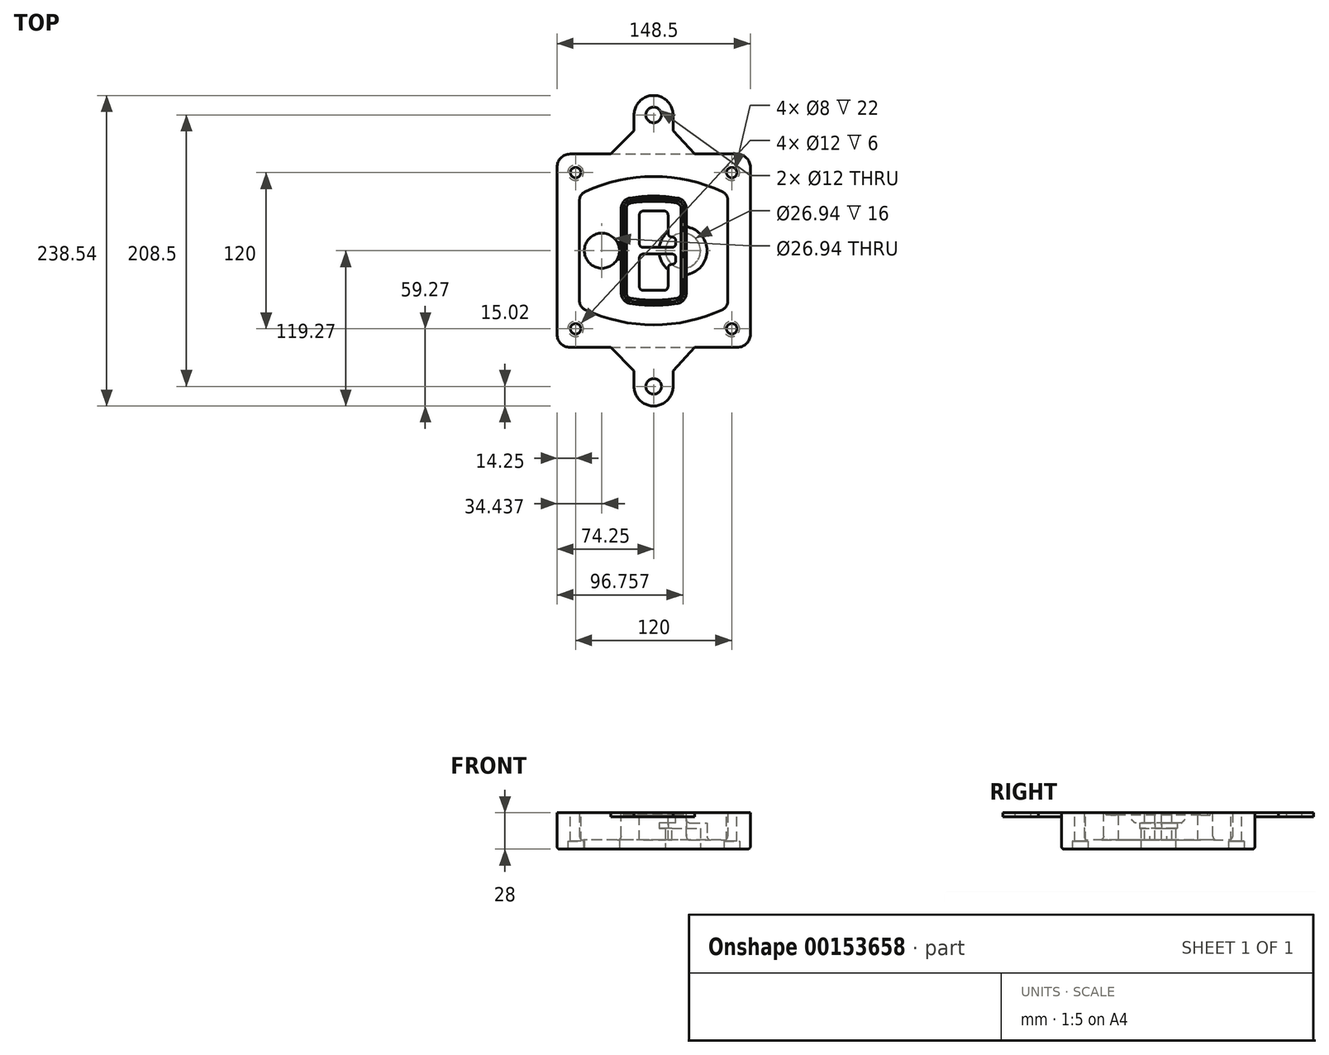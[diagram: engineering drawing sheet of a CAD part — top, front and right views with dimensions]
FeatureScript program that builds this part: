
annotation { "Feature Type Name" : "Feature", "Feature Type Description" : "" }
export const myFeature = defineFeature(function(context is Context, id is Id, definition is map)
    precondition{}
    {
        {
            var Q0;
            Q0=qCreatedBy(makeId("Top.planeOp"),FACE);
            var sketch = newSketch(context, id + "F0", { "sketchPlane" : qUnion([Q0])});
            skPoint(sketch, "E0.rect.middle", {"position": v(0, 0) * mm});
            skLineSegment(sketch, "E1.bottom", {"start": v(-64.25, -74.25) * mm, "end": v(64.25, -74.25) * mm});
            skLineSegment(sketch, "E1.top", {"start": v(-64.25, 74.25) * mm, "end": v(64.25, 74.25) * mm});
            skLineSegment(sketch, "E1.left", {"start": v(-74.25, -64.25) * mm, "end": v(-74.25, 64.25) * mm});
            skLineSegment(sketch, "E1.right", {"start": v(74.25, -64.25) * mm, "end": v(74.25, 64.25) * mm});
            skLineSegment(sketch, "E2", {"start": v(-74.25, 74.25) * mm, "end": v(74.25, -74.25) * mm, "construction": true});
            skLineSegment(sketch, "E3", {"start": v(74.25, 74.25) * mm, "end": v(-74.25, -74.25) * mm, "construction": true});
            skCircle(sketch, "E4", {"center": v(-60, 60) * mm, "radius": 4 * mm});
            skCircle(sketch, "E5", {"center": v(60, 60) * mm, "radius": 4 * mm});
            skCircle(sketch, "E6", {"center": v(60, -60) * mm, "radius": 4 * mm});
            skCircle(sketch, "E7", {"center": v(-60, -60) * mm, "radius": 4 * mm});
            skLineSegment(sketch, "E8", {"start": v(-60, 60) * mm, "end": v(60, 60) * mm, "construction": true});
            skLineSegment(sketch, "E9", {"start": v(60, 60) * mm, "end": v(60, -60) * mm, "construction": true});
            skLineSegment(sketch, "E10", {"start": v(60, -60) * mm, "end": v(-60, -60) * mm, "construction": true});
            skLineSegment(sketch, "E11", {"start": v(-60, -60) * mm, "end": v(-60, 60) * mm, "construction": true});
            skLineSegment(sketch, "E12", {"start": v(-60, 38.83) * mm, "end": v(-60, -38.83) * mm});
            skLineSegment(sketch, "E13", {"start": v(60, 38.83) * mm, "end": v(60, -38.83) * mm});
            skArc(sketch, "E14", {"start": v(54.26, 47.88) * mm, "mid": v(0, 60) * mm, "end": v(-54.26, 47.88) * mm});
            skArc(sketch, "E15", {"start": v(-54.26, -47.88) * mm, "mid": v(0, -60) * mm, "end": v(54.26, -47.88) * mm});
            skLineSegment(sketch, "E16", {"start": v(-60, 0) * mm, "end": v(60, 0) * mm, "construction": true});
            skPoint(sketch, "E17.visualSharp", {"position": v(-60, -45) * mm});
            skArc(sketch, "E17.filletArc", {"start": v(-60, -38.83) * mm, "mid": v(-58.44, -44.2) * mm, "end": v(-54.26, -47.88) * mm});
            skPoint(sketch, "E18.visualSharp", {"position": v(-60, 45) * mm});
            skArc(sketch, "E18.filletArc", {"start": v(-54.26, 47.88) * mm, "mid": v(-58.44, 44.2) * mm, "end": v(-60, 38.83) * mm});
            skPoint(sketch, "E19.visualSharp", {"position": v(60, 45) * mm});
            skArc(sketch, "E19.filletArc", {"start": v(60, 38.83) * mm, "mid": v(58.44, 44.2) * mm, "end": v(54.26, 47.88) * mm});
            skPoint(sketch, "E20.visualSharp", {"position": v(60, -45) * mm});
            skArc(sketch, "E20.filletArc", {"start": v(54.26, -47.88) * mm, "mid": v(58.44, -44.2) * mm, "end": v(60, -38.83) * mm});
            skPoint(sketch, "E21.visualSharp", {"position": v(-74.25, 74.25) * mm});
            skArc(sketch, "E21.filletArc", {"start": v(-64.25, 74.25) * mm, "mid": v(-71.32, 71.32) * mm, "end": v(-74.25, 64.25) * mm});
            skPoint(sketch, "E22.visualSharp", {"position": v(74.25, 74.25) * mm});
            skArc(sketch, "E22.filletArc", {"start": v(74.25, 64.25) * mm, "mid": v(71.32, 71.32) * mm, "end": v(64.25, 74.25) * mm});
            skPoint(sketch, "E23.visualSharp", {"position": v(74.25, -74.25) * mm});
            skArc(sketch, "E23.filletArc", {"start": v(64.25, -74.25) * mm, "mid": v(71.32, -71.32) * mm, "end": v(74.25, -64.25) * mm});
            skPoint(sketch, "E24.visualSharp", {"position": v(-74.25, -74.25) * mm});
            skArc(sketch, "E24.filletArc", {"start": v(-74.25, -64.25) * mm, "mid": v(-71.32, -71.32) * mm, "end": v(-64.25, -74.25) * mm});
            skArc(sketch, "E25.0", {"start": v(57, 38.83) * mm, "mid": v(55.9, 42.58) * mm, "end": v(52.98, 45.17) * mm});
            skLineSegment(sketch, "E25.1", {"start": v(57, 38.83) * mm, "end": v(57, -38.83) * mm});
            skArc(sketch, "E25.2", {"start": v(52.98, -45.17) * mm, "mid": v(55.9, -42.58) * mm, "end": v(57, -38.83) * mm});
            skArc(sketch, "E25.3", {"start": v(-52.98, -45.17) * mm, "mid": v(0, -57) * mm, "end": v(52.98, -45.17) * mm});
            skArc(sketch, "E25.4", {"start": v(-57, -38.83) * mm, "mid": v(-55.9, -42.58) * mm, "end": v(-52.98, -45.17) * mm});
            skArc(sketch, "E25.5", {"start": v(52.98, 45.17) * mm, "mid": v(0, 57) * mm, "end": v(-52.98, 45.17) * mm});
            skLineSegment(sketch, "E25.6", {"start": v(-57, 38.83) * mm, "end": v(-57, -38.83) * mm});
            skArc(sketch, "E25.7", {"start": v(-52.98, 45.17) * mm, "mid": v(-55.9, 42.58) * mm, "end": v(-57, 38.83) * mm});
            skArc(sketch, "E26.0", {"start": v(-55.96, 51.5) * mm, "mid": v(-61.82, 46.33) * mm, "end": v(-64, 38.83) * mm});
            skArc(sketch, "E26.1", {"start": v(55.96, 51.5) * mm, "mid": v(0, 64) * mm, "end": v(-55.96, 51.5) * mm});
            skArc(sketch, "E26.2", {"start": v(64, 38.83) * mm, "mid": v(61.82, 46.33) * mm, "end": v(55.96, 51.5) * mm});
            skLineSegment(sketch, "E26.3", {"start": v(64, 38.83) * mm, "end": v(64, -38.83) * mm});
            skArc(sketch, "E26.4", {"start": v(55.96, -51.5) * mm, "mid": v(61.82, -46.33) * mm, "end": v(64, -38.83) * mm});
            skLineSegment(sketch, "E26.5", {"start": v(-64, 38.83) * mm, "end": v(-64, -38.83) * mm});
            skArc(sketch, "E26.6", {"start": v(-55.96, -51.5) * mm, "mid": v(0, -64) * mm, "end": v(55.96, -51.5) * mm});
            skArc(sketch, "E26.7", {"start": v(-64, -38.83) * mm, "mid": v(-61.82, -46.33) * mm, "end": v(-55.96, -51.5) * mm});
            skSolve(sketch);
        }
        {
            var Q0;
            Q0=makeQuery(id+"F0.imprint","IMPRINT",FACE,{"disambiguationData":[TD([[makeQuery(id+"F0.imprint","IMPRINT",EDGE,{"derivedFrom":sQuery(id+"F0.wireOp",EDGE,"E1.bottom")}),1.0]])]});
            var Q1;
            Q1=makeQuery(id+"F0.imprint","IMPRINT",FACE,{"disambiguationData":[TD([[makeQuery(id+"F0.imprint","IMPRINT",EDGE,{"derivedFrom":sQuery(id+"F0.wireOp",EDGE,"E12")}),1.0]])]});
            var Q2;
            Q2=makeQuery(id+"F0.imprint","IMPRINT",FACE,{"disambiguationData":[TD([[makeQuery(id+"F0.imprint","IMPRINT",EDGE,{"derivedFrom":sQuery(id+"F0.wireOp",EDGE,"E25.0")}),1.0]])]});
            var Q3;
            Q3=makeQuery(id+"F0.imprint","IMPRINT",FACE,{"disambiguationData":[TD([[makeQuery(id+"F0.imprint","IMPRINT",EDGE,{"derivedFrom":sQuery(id+"F0.wireOp",EDGE,"E12")}),-1.0]])]});
            extrude(context, id + "F1", {"entities" : qUnion([Q0, Q1, Q2, Q3]), "oppositeDirection" : true, "depth" : 25 * mm});
        }
        {
            var Q0;
            Q0=makeQuery(id+"F0.imprint","IMPRINT",FACE,{"disambiguationData":[TD([[makeQuery(id+"F0.imprint","IMPRINT",EDGE,{"derivedFrom":sQuery(id+"F0.wireOp",EDGE,"E12")}),1.0]])]});
            extrude(context, id + "F2", {"entities" : qUnion([Q0]), "operationType" : NewBodyOperationType.ADD, "depth" : 3 * mm});
        }
        {
            var Q0;
            Q0=makeQuery(id+"F0.imprint","IMPRINT",FACE,{"disambiguationData":[TD([[makeQuery(id+"F0.imprint","IMPRINT",EDGE,{"derivedFrom":sQuery(id+"F0.wireOp",EDGE,"E25.0")}),1.0]])]});
            extrude(context, id + "F3", {"entities" : qUnion([Q0]), "operationType" : NewBodyOperationType.REMOVE, "oppositeDirection" : true, "depth" : 18 * mm});
        }
        {
            var Q0;
            Q0=makeQuery(id+"F2.opExtrude","CAP_FACE",FACE,{"disambiguationData":[OSD([sQuery(id+"F0.wireOp",EDGE,"E12"),sQuery(id+"F0.wireOp",EDGE,"E13"),sQuery(id+"F0.wireOp",EDGE,"E14"),sQuery(id+"F0.wireOp",EDGE,"E15"),sQuery(id+"F0.wireOp",EDGE,"E17.filletArc"),sQuery(id+"F0.wireOp",EDGE,"E18.filletArc"),sQuery(id+"F0.wireOp",EDGE,"E19.filletArc"),sQuery(id+"F0.wireOp",EDGE,"E20.filletArc"),sQuery(id+"F0.wireOp",EDGE,"E25.0"),sQuery(id+"F0.wireOp",EDGE,"E25.1"),sQuery(id+"F0.wireOp",EDGE,"E25.2"),sQuery(id+"F0.wireOp",EDGE,"E25.3"),sQuery(id+"F0.wireOp",EDGE,"E25.4"),sQuery(id+"F0.wireOp",EDGE,"E25.5"),sQuery(id+"F0.wireOp",EDGE,"E25.6"),sQuery(id+"F0.wireOp",EDGE,"E25.7")])],"isStart":false});
            var sketch = newSketch(context, id + "F4", { "sketchPlane" : qUnion([Q0])});
            skArc(sketch, "E27.0", {"start": v(-18.34, -40.45) * mm, "mid": v(0, -42) * mm, "end": v(18.34, -40.45) * mm});
            skArc(sketch, "E28.0", {"start": v(18.34, 40.45) * mm, "mid": v(0, 42) * mm, "end": v(-18.34, 40.45) * mm});
            skLineSegment(sketch, "E29", {"start": v(-25, 32.57) * mm, "end": v(-25, -32.57) * mm});
            skLineSegment(sketch, "E30", {"start": v(25, 32.57) * mm, "end": v(25, -32.57) * mm});
            skLineSegment(sketch, "E31", {"start": v(-25, 39.1) * mm, "end": v(25, 39.1) * mm, "construction": true});
            skLineSegment(sketch, "E32", {"start": v(-25, -39.1) * mm, "end": v(25, -39.1) * mm, "construction": true});
            skPoint(sketch, "E33.visualSharp", {"position": v(-25, 39.1) * mm});
            skArc(sketch, "E33.filletArc", {"start": v(-18.34, 40.45) * mm, "mid": v(-23.11, 37.73) * mm, "end": v(-25, 32.57) * mm});
            skPoint(sketch, "E34.visualSharp", {"position": v(25, 39.1) * mm});
            skArc(sketch, "E34.filletArc", {"start": v(25, 32.57) * mm, "mid": v(23.11, 37.73) * mm, "end": v(18.34, 40.45) * mm});
            skPoint(sketch, "E35.visualSharp", {"position": v(25, -39.1) * mm});
            skArc(sketch, "E35.filletArc", {"start": v(18.34, -40.45) * mm, "mid": v(23.11, -37.73) * mm, "end": v(25, -32.57) * mm});
            skPoint(sketch, "E36.visualSharp", {"position": v(-25, -39.1) * mm});
            skArc(sketch, "E36.filletArc", {"start": v(-25, -32.57) * mm, "mid": v(-23.11, -37.73) * mm, "end": v(-18.34, -40.45) * mm});
            skArc(sketch, "E37.0", {"start": v(52.98, 45.17) * mm, "mid": v(0, 57) * mm, "end": v(-52.98, 45.17) * mm});
            skArc(sketch, "E37.1", {"start": v(-52.98, 45.17) * mm, "mid": v(-55.9, 42.58) * mm, "end": v(-57, 38.83) * mm});
            skLineSegment(sketch, "E37.2", {"start": v(-57, 38.83) * mm, "end": v(-57, -38.83) * mm});
            skArc(sketch, "E37.3", {"start": v(-57, -38.83) * mm, "mid": v(-55.9, -42.58) * mm, "end": v(-52.98, -45.17) * mm});
            skArc(sketch, "E37.4", {"start": v(-52.98, -45.17) * mm, "mid": v(0, -57) * mm, "end": v(52.98, -45.17) * mm});
            skArc(sketch, "E37.5", {"start": v(52.98, -45.17) * mm, "mid": v(55.9, -42.58) * mm, "end": v(57, -38.83) * mm});
            skLineSegment(sketch, "E37.6", {"start": v(57, 38.83) * mm, "end": v(57, -38.83) * mm});
            skArc(sketch, "E37.7", {"start": v(57, 38.83) * mm, "mid": v(55.9, 42.58) * mm, "end": v(52.98, 45.17) * mm});
            skLineSegment(sketch, "E38.0", {"start": v(23, 32.57) * mm, "end": v(23, -32.57) * mm});
            skArc(sketch, "E38.1", {"start": v(18, -38.48) * mm, "mid": v(21.58, -36.44) * mm, "end": v(23, -32.57) * mm});
            skArc(sketch, "E38.2", {"start": v(-18, -38.48) * mm, "mid": v(0, -40) * mm, "end": v(18, -38.48) * mm});
            skArc(sketch, "E38.3", {"start": v(-23, -32.57) * mm, "mid": v(-21.58, -36.44) * mm, "end": v(-18, -38.48) * mm});
            skLineSegment(sketch, "E38.4", {"start": v(-23, 32.57) * mm, "end": v(-23, -32.57) * mm});
            skArc(sketch, "E38.5", {"start": v(23, 32.57) * mm, "mid": v(21.58, 36.44) * mm, "end": v(18, 38.48) * mm});
            skArc(sketch, "E38.6", {"start": v(-18, 38.48) * mm, "mid": v(-21.58, 36.44) * mm, "end": v(-23, 32.57) * mm});
            skArc(sketch, "E38.7", {"start": v(18, 38.48) * mm, "mid": v(0, 40) * mm, "end": v(-18, 38.48) * mm});
            skArc(sketch, "E39.0", {"start": v(21, 32.57) * mm, "mid": v(20.06, 35.15) * mm, "end": v(17.67, 36.5) * mm});
            skLineSegment(sketch, "E39.1", {"start": v(21, 32.57) * mm, "end": v(21, -32.57) * mm});
            skArc(sketch, "E39.2", {"start": v(17.67, -36.5) * mm, "mid": v(20.06, -35.15) * mm, "end": v(21, -32.57) * mm});
            skArc(sketch, "E39.3", {"start": v(-17.67, -36.5) * mm, "mid": v(0, -38) * mm, "end": v(17.67, -36.5) * mm});
            skArc(sketch, "E39.4", {"start": v(-21, -32.57) * mm, "mid": v(-20.06, -35.15) * mm, "end": v(-17.67, -36.5) * mm});
            skArc(sketch, "E39.5", {"start": v(17.67, 36.5) * mm, "mid": v(0, 38) * mm, "end": v(-17.67, 36.5) * mm});
            skLineSegment(sketch, "E39.6", {"start": v(-21, 32.57) * mm, "end": v(-21, -32.57) * mm});
            skArc(sketch, "E39.7", {"start": v(-17.67, 36.5) * mm, "mid": v(-20.06, 35.15) * mm, "end": v(-21, 32.57) * mm});
            skLineSegment(sketch, "E40", {"start": v(-25, 0) * mm, "end": v(25, 0) * mm, "construction": true});
            skLineSegment(sketch, "E41", {"start": v(-11, 5.5) * mm, "end": v(-11, 27.5) * mm});
            skLineSegment(sketch, "E42", {"start": v(-8, 30.5) * mm, "end": v(8, 30.5) * mm});
            skLineSegment(sketch, "E43", {"start": v(11, 27.5) * mm, "end": v(11, 13.5) * mm});
            skLineSegment(sketch, "E44", {"start": v(14, 10.5) * mm, "end": v(14, 10.5) * mm});
            skLineSegment(sketch, "E45", {"start": v(17, 7.5) * mm, "end": v(17, 5.5) * mm});
            skLineSegment(sketch, "E46", {"start": v(14, 2.5) * mm, "end": v(-8, 2.5) * mm});
            skPoint(sketch, "E47.visualSharp", {"position": v(-11, 30.5) * mm});
            skArc(sketch, "E47.filletArc", {"start": v(-8, 30.5) * mm, "mid": v(-10.12, 29.62) * mm, "end": v(-11, 27.5) * mm});
            skPoint(sketch, "E48.visualSharp", {"position": v(11, 30.5) * mm});
            skArc(sketch, "E48.filletArc", {"start": v(11, 27.5) * mm, "mid": v(10.12, 29.62) * mm, "end": v(8, 30.5) * mm});
            skPoint(sketch, "E49.visualSharp", {"position": v(11, 10.5) * mm});
            skArc(sketch, "E49.filletArc", {"start": v(11, 13.5) * mm, "mid": v(11.88, 11.38) * mm, "end": v(14, 10.5) * mm});
            skPoint(sketch, "E50.visualSharp", {"position": v(17, 10.5) * mm});
            skArc(sketch, "E50.filletArc", {"start": v(17, 7.5) * mm, "mid": v(16.12, 9.62) * mm, "end": v(14, 10.5) * mm});
            skPoint(sketch, "E51.visualSharp", {"position": v(17, 2.5) * mm});
            skArc(sketch, "E51.filletArc", {"start": v(14, 2.5) * mm, "mid": v(16.12, 3.38) * mm, "end": v(17, 5.5) * mm});
            skPoint(sketch, "E52.visualSharp", {"position": v(-11, 2.5) * mm});
            skArc(sketch, "E52.filletArc", {"start": v(-11, 5.5) * mm, "mid": v(-10.12, 3.38) * mm, "end": v(-8, 2.5) * mm});
            skLineSegment(sketch, "E53.0.MirrorCS", {"start": v(14, -2.5) * mm, "end": v(-8, -2.5) * mm});
            skArc(sketch, "E54.0.MirrorCS", {"start": v(-11, -5.5) * mm, "mid": v(-10.12, -3.38) * mm, "end": v(-8, -2.5) * mm});
            skLineSegment(sketch, "E55.0.MirrorCS", {"start": v(-11, -5.5) * mm, "end": v(-11, -27.5) * mm});
            skArc(sketch, "E56.0.MirrorCS", {"start": v(-8, -30.5) * mm, "mid": v(-10.12, -29.62) * mm, "end": v(-11, -27.5) * mm});
            skLineSegment(sketch, "E57.0.MirrorCS", {"start": v(-8, -30.5) * mm, "end": v(8, -30.5) * mm});
            skArc(sketch, "E58.0.MirrorCS", {"start": v(11, -27.5) * mm, "mid": v(10.12, -29.62) * mm, "end": v(8, -30.5) * mm});
            skLineSegment(sketch, "E59.0.MirrorCS", {"start": v(11, -27.5) * mm, "end": v(11, -13.5) * mm});
            skArc(sketch, "E60.0.MirrorCS", {"start": v(11, -13.5) * mm, "mid": v(11.88, -11.38) * mm, "end": v(14, -10.5) * mm});
            skArc(sketch, "E61.0.MirrorCS", {"start": v(17, -7.5) * mm, "mid": v(16.12, -9.62) * mm, "end": v(14, -10.5) * mm});
            skLineSegment(sketch, "E62.0.MirrorCS", {"start": v(17, -7.5) * mm, "end": v(17, -5.5) * mm});
            skArc(sketch, "E63.0.MirrorCS", {"start": v(14, -2.5) * mm, "mid": v(16.12, -3.38) * mm, "end": v(17, -5.5) * mm});
            skSolve(sketch);
        }
        {
            var Q0;
            Q0=makeQuery(id+"F4.imprint","IMPRINT",FACE,{"disambiguationData":[TD([[makeQuery(id+"F4.imprint","IMPRINT",EDGE,{"derivedFrom":sQuery(id+"F4.wireOp",EDGE,"E27.0")}),1.0]])]});
            var Q1;
            Q1=makeQuery(id+"F4.imprint","IMPRINT",FACE,{"disambiguationData":[TD([[makeQuery(id+"F4.imprint","IMPRINT",EDGE,{"derivedFrom":sQuery(id+"F4.wireOp",EDGE,"E38.0")}),-1.0]])]});
            var Q2;
            Q2=makeQuery(id+"F4.imprint","IMPRINT",FACE,{"disambiguationData":[TD([[makeQuery(id+"F4.imprint","IMPRINT",EDGE,{"derivedFrom":sQuery(id+"F4.wireOp",EDGE,"E39.0")}),1.0]])]});
            extrude(context, id + "F5", {"entities" : qUnion([Q0, Q1, Q2]), "operationType" : NewBodyOperationType.ADD, "endBound" : BoundingType.UP_TO_NEXT, "oppositeDirection" : true, "depth" : 25 * mm});
        }
        {
            var Q0;
            Q0=makeQuery(id+"F4.imprint","IMPRINT",FACE,{"disambiguationData":[TD([[makeQuery(id+"F4.imprint","IMPRINT",EDGE,{"derivedFrom":sQuery(id+"F4.wireOp",EDGE,"E38.0")}),-1.0]])]});
            extrude(context, id + "F6", {"entities" : qUnion([Q0]), "operationType" : NewBodyOperationType.REMOVE, "oppositeDirection" : true, "depth" : 2 * mm});
        }
        {
            var Q0;
            Q0=makeQuery(id+"F1.opExtrude","CAP_FACE",FACE,{"disambiguationData":[OSD([sQuery(id+"F0.wireOp",EDGE,"E1.bottom"),sQuery(id+"F0.wireOp",EDGE,"E1.top"),sQuery(id+"F0.wireOp",EDGE,"E1.left"),sQuery(id+"F0.wireOp",EDGE,"E1.right"),sQuery(id+"F0.wireOp",EDGE,"E4"),sQuery(id+"F0.wireOp",EDGE,"E5"),sQuery(id+"F0.wireOp",EDGE,"E6"),sQuery(id+"F0.wireOp",EDGE,"E7"),sQuery(id+"F0.wireOp",EDGE,"E21.filletArc"),sQuery(id+"F0.wireOp",EDGE,"E22.filletArc"),sQuery(id+"F0.wireOp",EDGE,"E23.filletArc"),sQuery(id+"F0.wireOp",EDGE,"E24.filletArc")])],"isStart":false});
            var sketch = newSketch(context, id + "F7", { "sketchPlane" : qUnion([Q0])});
            skCircle(sketch, "E64", {"center": v(22.5, 0) * mm, "radius": 13.47 * mm});
            skCircle(sketch, "E65", {"center": v(-39.81, 0) * mm, "radius": 13.47 * mm});
            skLineSegment(sketch, "E66", {"start": v(74.25, 0) * mm, "end": v(-74.25, 0) * mm});
            skCircle(sketch, "E67", {"center": v(22.5, 0) * mm, "radius": 18.47 * mm});
            skCircle(sketch, "E68", {"center": v(60, -60) * mm, "radius": 6 * mm});
            skCircle(sketch, "E69", {"center": v(-60, -60) * mm, "radius": 6 * mm});
            skCircle(sketch, "E70", {"center": v(-60, 60) * mm, "radius": 6 * mm});
            skCircle(sketch, "E71", {"center": v(60, 60) * mm, "radius": 6 * mm});
            skSolve(sketch);
        }
        {
            var Q0;
            {var subQ1=sQuery(id+"F7.wireOp",EDGE,"E66");var subQ4=sQuery(id+"F7.wireOp",EDGE,"E64");var subQ6=makeQuery(id+"F7.imprint","INTERSECT",VERTEX,{"disambiguationData":[OD(0.0)],"derivedFrom":[subQ4,subQ1]});Q0=makeQuery(id+"F7.imprint","IMPRINT",FACE,{"disambiguationData":[TD([[makeQuery(id+"F7.imprint","IMPRINT",EDGE,{"disambiguationData":[TD([[subQ6,-1.0]])],"derivedFrom":subQ4}),-1.0]])]});}
            var Q1;
            {var subQ0=sQuery(id+"F7.wireOp",EDGE,"E66");var subQ1=sQuery(id+"F7.wireOp",EDGE,"E64");var subQ3=makeQuery(id+"F7.imprint","INTERSECT",VERTEX,{"disambiguationData":[OD(0.0)],"derivedFrom":[subQ1,subQ0]});Q1=makeQuery(id+"F7.imprint","IMPRINT",FACE,{"disambiguationData":[TD([[makeQuery(id+"F7.imprint","IMPRINT",EDGE,{"disambiguationData":[TD([[subQ3,-1.0]])],"derivedFrom":subQ1}),1.0]])]});}
            var Q2;
            {var subQ0=sQuery(id+"F7.wireOp",EDGE,"E66");var subQ1=sQuery(id+"F7.wireOp",EDGE,"E64");var subQ3=makeQuery(id+"F7.imprint","INTERSECT",VERTEX,{"disambiguationData":[OD(0.0)],"derivedFrom":[subQ1,subQ0]});Q2=makeQuery(id+"F7.imprint","IMPRINT",FACE,{"disambiguationData":[TD([[makeQuery(id+"F7.imprint","IMPRINT",EDGE,{"disambiguationData":[TD([[subQ3,1.0]])],"derivedFrom":subQ1}),1.0]])]});}
            var Q3;
            {var subQ1=sQuery(id+"F7.wireOp",EDGE,"E66");var subQ4=sQuery(id+"F7.wireOp",EDGE,"E64");var subQ6=makeQuery(id+"F7.imprint","INTERSECT",VERTEX,{"disambiguationData":[OD(0.0)],"derivedFrom":[subQ4,subQ1]});Q3=makeQuery(id+"F7.imprint","IMPRINT",FACE,{"disambiguationData":[TD([[makeQuery(id+"F7.imprint","IMPRINT",EDGE,{"disambiguationData":[TD([[subQ6,1.0]])],"derivedFrom":subQ4}),-1.0]])]});}
            extrude(context, id + "F8", {"entities" : qUnion([Q0, Q1, Q2, Q3]), "operationType" : NewBodyOperationType.ADD, "oppositeDirection" : true, "depth" : 20 * mm});
        }
        {
            var Q0;
            {var subQ0=sQuery(id+"F7.wireOp",EDGE,"E66");var subQ1=sQuery(id+"F7.wireOp",EDGE,"E64");var subQ3=makeQuery(id+"F7.imprint","INTERSECT",VERTEX,{"disambiguationData":[OD(0.0)],"derivedFrom":[subQ1,subQ0]});Q0=makeQuery(id+"F7.imprint","IMPRINT",FACE,{"disambiguationData":[TD([[makeQuery(id+"F7.imprint","IMPRINT",EDGE,{"disambiguationData":[TD([[subQ3,-1.0]])],"derivedFrom":subQ1}),1.0]])]});}
            var Q1;
            {var subQ0=sQuery(id+"F7.wireOp",EDGE,"E66");var subQ1=sQuery(id+"F7.wireOp",EDGE,"E64");var subQ3=makeQuery(id+"F7.imprint","INTERSECT",VERTEX,{"disambiguationData":[OD(0.0)],"derivedFrom":[subQ1,subQ0]});Q1=makeQuery(id+"F7.imprint","IMPRINT",FACE,{"disambiguationData":[TD([[makeQuery(id+"F7.imprint","IMPRINT",EDGE,{"disambiguationData":[TD([[subQ3,1.0]])],"derivedFrom":subQ1}),1.0]])]});}
            extrude(context, id + "F9", {"entities" : qUnion([Q0, Q1]), "operationType" : NewBodyOperationType.REMOVE, "oppositeDirection" : true, "depth" : 16 * mm});
        }
        {
            var Q0;
            {var subQ0=sQuery(id+"F7.wireOp",EDGE,"E66");var subQ1=sQuery(id+"F7.wireOp",EDGE,"E65");var subQ3=makeQuery(id+"F7.imprint","INTERSECT",VERTEX,{"disambiguationData":[OD(0.0)],"derivedFrom":[subQ1,subQ0]});Q0=makeQuery(id+"F7.imprint","IMPRINT",FACE,{"disambiguationData":[TD([[makeQuery(id+"F7.imprint","IMPRINT",EDGE,{"disambiguationData":[TD([[subQ3,-1.0]])],"derivedFrom":subQ1}),1.0]])]});}
            var Q1;
            {var subQ0=sQuery(id+"F7.wireOp",EDGE,"E66");var subQ1=sQuery(id+"F7.wireOp",EDGE,"E65");var subQ3=makeQuery(id+"F7.imprint","INTERSECT",VERTEX,{"disambiguationData":[OD(0.0)],"derivedFrom":[subQ1,subQ0]});Q1=makeQuery(id+"F7.imprint","IMPRINT",FACE,{"disambiguationData":[TD([[makeQuery(id+"F7.imprint","IMPRINT",EDGE,{"disambiguationData":[TD([[subQ3,1.0]])],"derivedFrom":subQ1}),1.0]])]});}
            extrude(context, id + "F10", {"entities" : qUnion([Q0, Q1]), "operationType" : NewBodyOperationType.REMOVE, "oppositeDirection" : true, "depth" : 25 * mm});
        }
        {
            var Q0;
            Q0=makeQuery(id+"F7.imprint","IMPRINT",FACE,{"disambiguationData":[TD([[makeQuery(id+"F7.imprint","IMPRINT",EDGE,{"derivedFrom":sQuery(id+"F7.wireOp",EDGE,"E68")}),1.0]])]});
            var Q1;
            Q1=makeQuery(id+"F7.imprint","IMPRINT",FACE,{"disambiguationData":[TD([[makeQuery(id+"F7.imprint","IMPRINT",EDGE,{"derivedFrom":makeQuery(id+"F1.opExtrude","CAP_EDGE",EDGE,{"disambiguationData":[OSD([sQuery(id+"F0.wireOp",EDGE,"E5")])],"isStart":false})}),-1.0]])]});
            var Q2;
            Q2=makeQuery(id+"F7.imprint","IMPRINT",FACE,{"disambiguationData":[TD([[makeQuery(id+"F7.imprint","IMPRINT",EDGE,{"derivedFrom":sQuery(id+"F7.wireOp",EDGE,"E69")}),1.0]])]});
            var Q3;
            Q3=makeQuery(id+"F7.imprint","IMPRINT",FACE,{"disambiguationData":[TD([[makeQuery(id+"F7.imprint","IMPRINT",EDGE,{"derivedFrom":makeQuery(id+"F1.opExtrude","CAP_EDGE",EDGE,{"disambiguationData":[OSD([sQuery(id+"F0.wireOp",EDGE,"E4")])],"isStart":false})}),-1.0]])]});
            var Q4;
            Q4=makeQuery(id+"F7.imprint","IMPRINT",FACE,{"disambiguationData":[TD([[makeQuery(id+"F7.imprint","IMPRINT",EDGE,{"derivedFrom":sQuery(id+"F7.wireOp",EDGE,"E70")}),1.0]])]});
            var Q5;
            Q5=makeQuery(id+"F7.imprint","IMPRINT",FACE,{"disambiguationData":[TD([[makeQuery(id+"F7.imprint","IMPRINT",EDGE,{"derivedFrom":makeQuery(id+"F1.opExtrude","CAP_EDGE",EDGE,{"disambiguationData":[OSD([sQuery(id+"F0.wireOp",EDGE,"E7")])],"isStart":false})}),-1.0]])]});
            var Q6;
            Q6=makeQuery(id+"F7.imprint","IMPRINT",FACE,{"disambiguationData":[TD([[makeQuery(id+"F7.imprint","IMPRINT",EDGE,{"derivedFrom":sQuery(id+"F7.wireOp",EDGE,"E71")}),1.0]])]});
            var Q7;
            Q7=makeQuery(id+"F7.imprint","IMPRINT",FACE,{"disambiguationData":[TD([[makeQuery(id+"F7.imprint","IMPRINT",EDGE,{"derivedFrom":makeQuery(id+"F1.opExtrude","CAP_EDGE",EDGE,{"disambiguationData":[OSD([sQuery(id+"F0.wireOp",EDGE,"E6")])],"isStart":false})}),-1.0]])]});
            extrude(context, id + "F11", {"entities" : qUnion([Q0, Q1, Q2, Q3, Q4, Q5, Q6, Q7]), "operationType" : NewBodyOperationType.REMOVE, "oppositeDirection" : true, "depth" : 6 * mm});
        }
        {
            var Q0;
            Q0=makeQuery(id+"F9.boolean.opBoolean","COPY",FACE,{"derivedFrom":makeQuery(id+"F9.opExtrude","CAP_FACE",FACE,{"disambiguationData":[OSD([sQuery(id+"F7.wireOp",EDGE,"E64")])],"isStart":false})});
            var sketch = newSketch(context, id + "F12", { "sketchPlane" : qUnion([Q0])});
            skArc(sketch, "E72.0", {"start": v(11, 14.45) * mm, "mid": v(6.45, 9.13) * mm, "end": v(4.2, 2.5) * mm});
            skArc(sketch, "E72.1", {"start": v(4.2, -2.5) * mm, "mid": v(6.45, -9.13) * mm, "end": v(11, -14.45) * mm});
            skLineSegment(sketch, "E73", {"start": v(4.2, -2.5) * mm, "end": v(14, -2.5) * mm});
            skLineSegment(sketch, "E74.0", {"start": v(14, 2.5) * mm, "end": v(4.2, 2.5) * mm});
            skArc(sketch, "E74.1", {"start": v(14, 2.5) * mm, "mid": v(16.12, 3.38) * mm, "end": v(17, 5.5) * mm});
            skLineSegment(sketch, "E74.2", {"start": v(17, 7.5) * mm, "end": v(17, 5.5) * mm});
            skArc(sketch, "E74.3", {"start": v(17, 7.5) * mm, "mid": v(16.12, 9.62) * mm, "end": v(14, 10.5) * mm});
            skArc(sketch, "E74.4", {"start": v(11, 13.5) * mm, "mid": v(11.88, 11.38) * mm, "end": v(14, 10.5) * mm});
            skLineSegment(sketch, "E74.5", {"start": v(11, 14.45) * mm, "end": v(11, 13.5) * mm});
            skLineSegment(sketch, "E74.7", {"start": v(14, -2.5) * mm, "end": v(4.2, -2.5) * mm});
            skArc(sketch, "E74.8", {"start": v(14, -2.5) * mm, "mid": v(16.12, -3.38) * mm, "end": v(17, -5.5) * mm});
            skLineSegment(sketch, "E74.9", {"start": v(17, -7.5) * mm, "end": v(17, -5.5) * mm});
            skArc(sketch, "E74.10", {"start": v(17, -7.5) * mm, "mid": v(16.12, -9.62) * mm, "end": v(14, -10.5) * mm});
            skArc(sketch, "E74.11", {"start": v(11, -13.5) * mm, "mid": v(11.88, -11.38) * mm, "end": v(14, -10.5) * mm});
            skLineSegment(sketch, "E74.12", {"start": v(11, -14.45) * mm, "end": v(11, -13.5) * mm});
            skPoint(sketch, "E75.orphan", {"position": v(11, -27.5) * mm});
            skPoint(sketch, "E76.orphan", {"position": v(-8, -2.5) * mm});
            skPoint(sketch, "E77.orphan", {"position": v(-8, 2.5) * mm});
            skPoint(sketch, "E78.orphan", {"position": v(11, 27.5) * mm});
            skSolve(sketch);
        }
        {
            var Q0;
            {var subQ7=sQuery(id+"F12.wireOp",EDGE,"E72.0");var subQ14=sQuery(id+"F12.wireOp",EDGE,"E72.1");var subQ16=sQuery(id+"F12.wireOp",EDGE,"E74.1");var subQ18=sQuery(id+"F12.wireOp",EDGE,"E74.8");Q0=qUnion([makeQuery(id+"F12.imprint","IMPRINT",FACE,{"disambiguationData":[TD([[makeQuery(id+"F12.imprint","IMPRINT",EDGE,{"derivedFrom":subQ7}),1.0]])]}),makeQuery(id+"F12.imprint","IMPRINT",FACE,{"disambiguationData":[TD([[makeQuery(id+"F12.imprint","IMPRINT",EDGE,{"derivedFrom":subQ14}),1.0]])]}),makeQuery(id+"F12.imprint","IMPRINT",FACE,{"disambiguationData":[TD([[makeQuery(id+"F12.imprint","IMPRINT",EDGE,{"derivedFrom":subQ16}),1.0]])]}),makeQuery(id+"F12.imprint","IMPRINT",FACE,{"disambiguationData":[TD([[makeQuery(id+"F12.imprint","IMPRINT",EDGE,{"derivedFrom":subQ18}),-1.0]])]})]);}
            var Q1;
            Q1=makeQuery(id+"F5.boolean.opBoolean","SPLIT",FACE,{"disambiguationData":[TD([makeQuery(id+"F5.opExtrude","SWEPT_FACE",FACE,{"disambiguationData":[OSD([sQuery(id+"F4.wireOp",EDGE,"E41")])]})])],"derivedFrom":makeQuery(id+"F3.boolean.opBoolean","COPY",FACE,{"derivedFrom":makeQuery(id+"F3.opExtrude","CAP_FACE",FACE,{"disambiguationData":[OSD([sQuery(id+"F0.wireOp",EDGE,"E25.0"),sQuery(id+"F0.wireOp",EDGE,"E25.1"),sQuery(id+"F0.wireOp",EDGE,"E25.2"),sQuery(id+"F0.wireOp",EDGE,"E25.3"),sQuery(id+"F0.wireOp",EDGE,"E25.4"),sQuery(id+"F0.wireOp",EDGE,"E25.5"),sQuery(id+"F0.wireOp",EDGE,"E25.6"),sQuery(id+"F0.wireOp",EDGE,"E25.7")])],"isStart":false})})});
            extrude(context, id + "F13", {"entities" : qUnion([Q0]), "operationType" : NewBodyOperationType.REMOVE, "endBound" : BoundingType.UP_TO_SURFACE, "endBoundEntityFace" : qUnion([Q1]), "depth" : 25 * mm});
        }
        {
            var Q0;
            Q0=makeQuery(id+"F3.boolean.opBoolean","COPY",EDGE,{"derivedFrom":makeQuery(id+"F3.opExtrude","CAP_EDGE",EDGE,{"disambiguationData":[OSD([sQuery(id+"F0.wireOp",EDGE,"E25.6")])],"isStart":false})});
            var Q1;
            Q1=makeQuery(id+"F8.boolean.opBoolean","INTERSECT",EDGE,{"derivedFrom":[makeQuery(id+"F5.opExtrude","SWEPT_FACE",FACE,{"disambiguationData":[OSD([sQuery(id+"F4.wireOp",EDGE,"E30")])]}),makeQuery(id+"F8.opExtrude","CAP_FACE",FACE,{"disambiguationData":[OSD([sQuery(id+"F7.wireOp",EDGE,"E67")])],"isStart":false})]});
            var Q2;
            Q2=makeQuery(id+"F8.boolean.opBoolean","INTERSECT",EDGE,{"disambiguationData":[OD(1.0)],"derivedFrom":[makeQuery(id+"F5.opExtrude","SWEPT_FACE",FACE,{"disambiguationData":[OSD([sQuery(id+"F4.wireOp",EDGE,"E30")])]}),makeQuery(id+"F8.opExtrude","SWEPT_FACE",FACE,{"disambiguationData":[OSD([sQuery(id+"F7.wireOp",EDGE,"E67")])]})]});
            var Q3;
            {var subQ0=sQuery(id+"F4.wireOp",EDGE,"E30");Q3=makeQuery(id+"F8.boolean.opBoolean","SPLIT",EDGE,{"disambiguationData":[TD([makeQuery(id+"F5.opExtrude","SWEPT_FACE",FACE,{"disambiguationData":[OSD([sQuery(id+"F4.wireOp",EDGE,"E35.filletArc")])]})])],"derivedFrom":makeQuery(id+"F5.opExtrude","CAP_EDGE",EDGE,{"disambiguationData":[OSD([subQ0])],"isStart":false})});}
            var Q4;
            {var subQ0=sQuery(id+"F0.wireOp",EDGE,"E25.7");var subQ1=sQuery(id+"F0.wireOp",EDGE,"E25.1");var subQ2=sQuery(id+"F0.wireOp",EDGE,"E25.6");var subQ3=sQuery(id+"F0.wireOp",EDGE,"E25.5");var subQ4=sQuery(id+"F0.wireOp",EDGE,"E25.4");var subQ5=sQuery(id+"F0.wireOp",EDGE,"E25.0");var subQ6=sQuery(id+"F0.wireOp",EDGE,"E25.2");var subQ7=sQuery(id+"F0.wireOp",EDGE,"E25.3");Q4=makeQuery(id+"F8.boolean.opBoolean","INTERSECT",EDGE,{"derivedFrom":[makeQuery(id+"F5.boolean.opBoolean","SPLIT",FACE,{"disambiguationData":[TD([makeQuery(id+"F2.opExtrude","SWEPT_FACE",FACE,{"disambiguationData":[OSD([subQ5])]})])],"derivedFrom":makeQuery(id+"F3.boolean.opBoolean","COPY",FACE,{"derivedFrom":makeQuery(id+"F3.opExtrude","CAP_FACE",FACE,{"disambiguationData":[OSD([subQ5,subQ1,subQ6,subQ7,subQ4,subQ3,subQ2,subQ0])],"isStart":false})})}),makeQuery(id+"F8.opExtrude","SWEPT_FACE",FACE,{"disambiguationData":[OSD([sQuery(id+"F7.wireOp",EDGE,"E67")])]})]});}
            var Q5;
            Q5=makeQuery(id+"F8.boolean.opBoolean","INTERSECT",EDGE,{"disambiguationData":[OD(0.0)],"derivedFrom":[makeQuery(id+"F5.opExtrude","SWEPT_FACE",FACE,{"disambiguationData":[OSD([sQuery(id+"F4.wireOp",EDGE,"E30")])]}),makeQuery(id+"F8.opExtrude","SWEPT_FACE",FACE,{"disambiguationData":[OSD([sQuery(id+"F7.wireOp",EDGE,"E67")])]})]});
            fillet(context, id + "F14", {"entities" : qUnion([Q0, Q1, Q2, Q3, Q4, Q5]), "radius" : 3 * mm, "tangentPropagation" : true, "allowEdgeOverflow" : false});
        }
        {
            var Q0;
            Q0=makeQuery(id+"F1.opExtrude","CAP_EDGE",EDGE,{"disambiguationData":[OSD([sQuery(id+"F0.wireOp",EDGE,"E1.bottom")])],"isStart":false});
            fillet(context, id + "F15", {"entities" : qUnion([Q0]), "radius" : 2 * mm, "tangentPropagation" : true, "allowEdgeOverflow" : false});
        }
        {
            var Q0;
            {var subQ0=sQuery(id+"F0.wireOp",EDGE,"E22.filletArc");var subQ1=sQuery(id+"F0.wireOp",EDGE,"E7");var subQ2=sQuery(id+"F0.wireOp",EDGE,"E6");var subQ3=sQuery(id+"F0.wireOp",EDGE,"E5");var subQ4=sQuery(id+"F0.wireOp",EDGE,"E4");var subQ5=sQuery(id+"F0.wireOp",EDGE,"E1.bottom");var subQ6=sQuery(id+"F0.wireOp",EDGE,"E21.filletArc");var subQ7=sQuery(id+"F0.wireOp",EDGE,"E1.top");var subQ8=sQuery(id+"F0.wireOp",EDGE,"E1.left");var subQ9=sQuery(id+"F0.wireOp",EDGE,"E1.right");var subQ10=sQuery(id+"F0.wireOp",EDGE,"E23.filletArc");var subQ11=sQuery(id+"F0.wireOp",EDGE,"E24.filletArc");Q0=makeQuery(id+"F2.boolean.opBoolean","SPLIT",FACE,{"disambiguationData":[TD([makeQuery(id+"F1.opExtrude","SWEPT_FACE",FACE,{"disambiguationData":[OSD([subQ5])]})])],"derivedFrom":makeQuery(id+"F1.opExtrude","CAP_FACE",FACE,{"disambiguationData":[OSD([subQ5,subQ7,subQ8,subQ9,subQ4,subQ3,subQ2,subQ1,subQ6,subQ0,subQ10,subQ11])],"isStart":true})});}
            var sketch = newSketch(context, id + "F16", { "sketchPlane" : qUnion([Q0])});
            skLineSegment(sketch, "E79.0", {"start": v(-64.25, 74.25) * mm, "end": v(64.25, 74.25) * mm});
            skLineSegment(sketch, "E80.0", {"start": v(-74.25, -64.25) * mm, "end": v(-74.25, 64.25) * mm});
            skLineSegment(sketch, "E81.0", {"start": v(74.25, -64.25) * mm, "end": v(74.25, 64.25) * mm});
            skLineSegment(sketch, "E82.0", {"start": v(-64.25, -74.25) * mm, "end": v(64.25, -74.25) * mm});
            skLineSegment(sketch, "E83", {"start": v(-74.25, 0) * mm, "end": v(74.25, 0) * mm, "construction": true});
            skLineSegment(sketch, "E84", {"start": v(0, 74.25) * mm, "end": v(0, 104.25) * mm, "construction": true});
            skCircle(sketch, "E85", {"center": v(0, 104.25) * mm, "radius": 6 * mm});
            skArc(sketch, "E86", {"start": v(14.9, 104.25) * mm, "mid": v(-0.1, 119.27) * mm, "end": v(-15.1, 104.25) * mm});
            skLineSegment(sketch, "E87", {"start": v(-15.1, 104.25) * mm, "end": v(-15.09, 92.25) * mm});
            skLineSegment(sketch, "E88", {"start": v(-15.09, 92.25) * mm, "end": v(-33.09, 74.25) * mm});
            skLineSegment(sketch, "E89", {"start": v(14.9, 104.25) * mm, "end": v(14.9, 92.25) * mm});
            skLineSegment(sketch, "E90", {"start": v(14.9, 92.25) * mm, "end": v(31.34, 74.25) * mm});
            skLineSegment(sketch, "E91.MirrorCS", {"start": v(14.9, -104.25) * mm, "end": v(14.9, -92.25) * mm});
            skLineSegment(sketch, "E92.MirrorCS", {"start": v(-15.1, -104.25) * mm, "end": v(-15.09, -92.25) * mm});
            skLineSegment(sketch, "E93.MirrorCS", {"start": v(14.9, -92.25) * mm, "end": v(31.34, -74.25) * mm});
            skLineSegment(sketch, "E94.MirrorCS", {"start": v(-15.09, -92.25) * mm, "end": v(-33.09, -74.25) * mm});
            skArc(sketch, "E95.MirrorCS", {"start": v(14.9, -104.25) * mm, "mid": v(-0.1, -119.27) * mm, "end": v(-15.1, -104.25) * mm});
            skCircle(sketch, "E96.MirrorC", {"center": v(0, -104.25) * mm, "radius": 6 * mm});
            skLineSegment(sketch, "E97.MirrorCS", {"start": v(0, -74.25) * mm, "end": v(0, -104.25) * mm, "construction": true});
            skSolve(sketch);
        }
        {
            var Q0;
            Q0=makeQuery(id+"F16.imprint","IMPRINT",FACE,{"disambiguationData":[TD([[makeQuery(id+"F16.imprint","IMPRINT",EDGE,{"derivedFrom":sQuery(id+"F16.wireOp",EDGE,"E85")}),-1.0]])]});
            var Q1;
            Q1=makeQuery(id+"F16.imprint","IMPRINT",FACE,{"disambiguationData":[TD([[makeQuery(id+"F16.imprint","IMPRINT",EDGE,{"derivedFrom":sQuery(id+"F16.wireOp",EDGE,"E80.0")}),-1.0]])]});
            var Q2;
            Q2=makeQuery(id+"F16.imprint","IMPRINT",FACE,{"disambiguationData":[TD([[makeQuery(id+"F16.imprint","IMPRINT",EDGE,{"derivedFrom":sQuery(id+"F16.wireOp",EDGE,"E91.MirrorCS")}),1.0]])]});
            var Q3;
            Q3=makeQuery(id+"F2.opExtrude","CAP_FACE",FACE,{"disambiguationData":[OSD([sQuery(id+"F0.wireOp",EDGE,"E12"),sQuery(id+"F0.wireOp",EDGE,"E13"),sQuery(id+"F0.wireOp",EDGE,"E14"),sQuery(id+"F0.wireOp",EDGE,"E15"),sQuery(id+"F0.wireOp",EDGE,"E17.filletArc"),sQuery(id+"F0.wireOp",EDGE,"E18.filletArc"),sQuery(id+"F0.wireOp",EDGE,"E19.filletArc"),sQuery(id+"F0.wireOp",EDGE,"E20.filletArc"),sQuery(id+"F0.wireOp",EDGE,"E25.0"),sQuery(id+"F0.wireOp",EDGE,"E25.1"),sQuery(id+"F0.wireOp",EDGE,"E25.2"),sQuery(id+"F0.wireOp",EDGE,"E25.3"),sQuery(id+"F0.wireOp",EDGE,"E25.4"),sQuery(id+"F0.wireOp",EDGE,"E25.5"),sQuery(id+"F0.wireOp",EDGE,"E25.6"),sQuery(id+"F0.wireOp",EDGE,"E25.7")])],"isStart":false});
            extrude(context, id + "F17", {"entities" : qUnion([Q0, Q1, Q2]), "operationType" : NewBodyOperationType.ADD, "endBound" : BoundingType.UP_TO_SURFACE, "endBoundEntityFace" : qUnion([Q3]), "depth" : 25 * mm});
        }
    });
